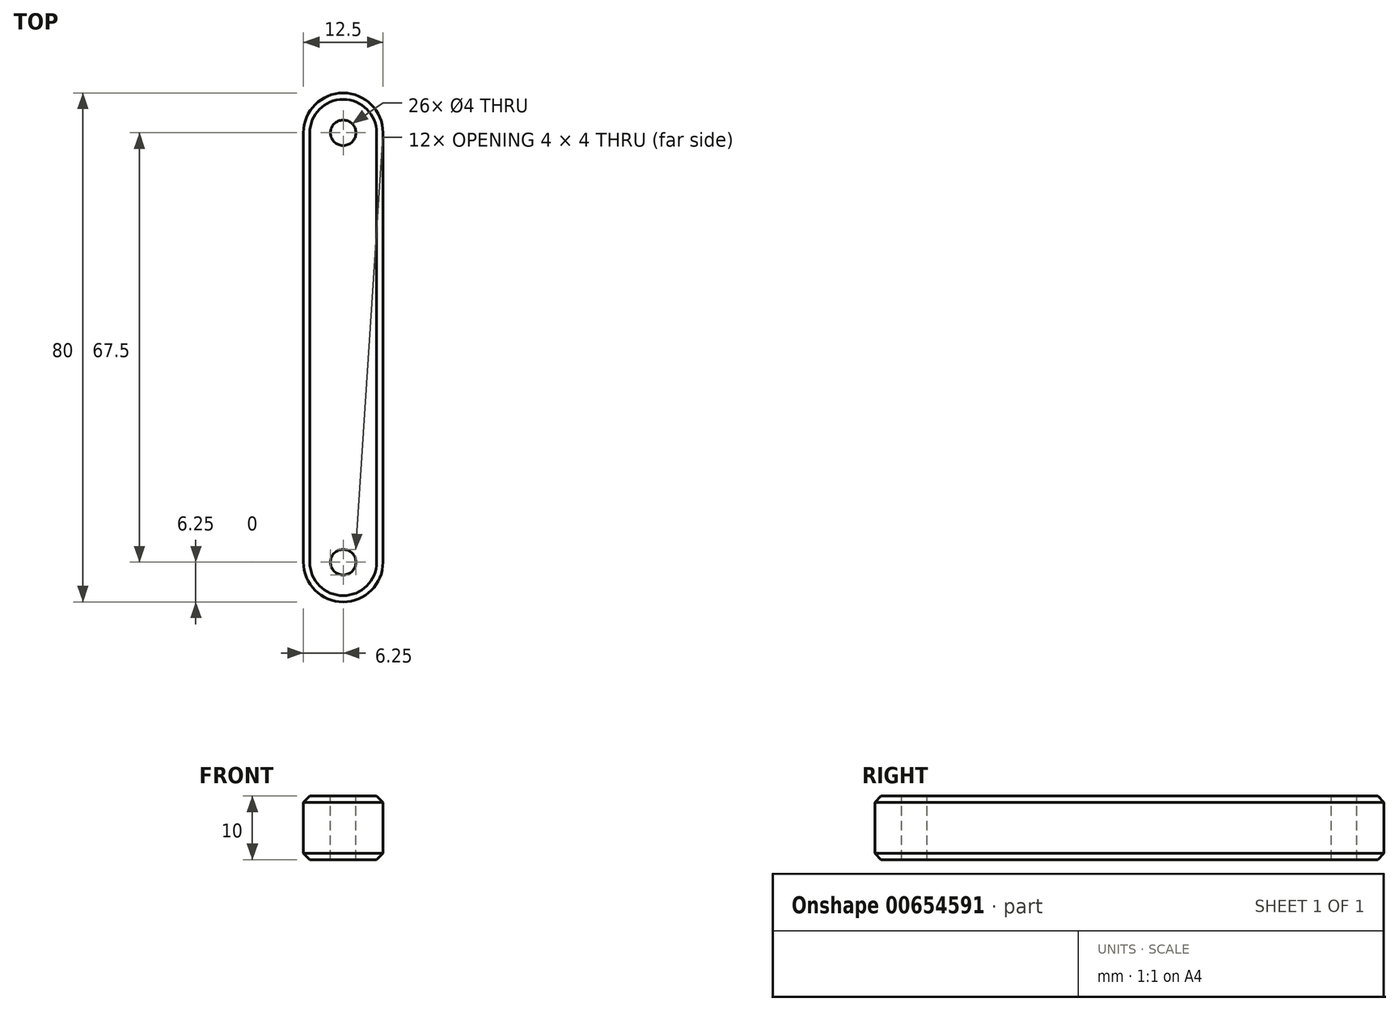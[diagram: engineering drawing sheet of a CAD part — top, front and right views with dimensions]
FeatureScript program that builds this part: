
annotation { "Feature Type Name" : "Feature", "Feature Type Description" : "" }
export const myFeature = defineFeature(function(context is Context, id is Id, definition is map)
    precondition{}
    {
        {
            var Q0;
            Q0=qCreatedBy(makeId("Front.planeOp"),FACE);
            var sketch = newSketch(context, id + "F0", { "sketchPlane" : qUnion([Q0])});
            skLineSegment(sketch, "E0.bottom", {"start": v(0, 0) * mm, "end": v(12.5, 0) * mm});
            skLineSegment(sketch, "E0.top", {"start": v(0, 10) * mm, "end": v(12.5, 10) * mm});
            skLineSegment(sketch, "E0.left", {"start": v(0, 0) * mm, "end": v(0, 10) * mm});
            skLineSegment(sketch, "E0.right", {"start": v(12.5, 0) * mm, "end": v(12.5, 10) * mm});
            skSolve(sketch);
        }
        {
            var Q0;
            Q0=makeQuery(id+"F0.imprint","IMPRINT",FACE,{"disambiguationData":[TD([[makeQuery(id+"F0.imprint","IMPRINT",EDGE,{"derivedFrom":sQuery(id+"F0.wireOp",EDGE,"E0.bottom")}),1.0]])]});
            extrude(context, id + "F1", {"entities" : qUnion([Q0]), "oppositeDirection" : true, "depth" : 80 * mm, "offsetDistance" : 25 * mm});
        }
        {
            var Q0;
            Q0=makeQuery(id+"F1.opExtrude","SWEPT_FACE",FACE,{"disambiguationData":[OSD([sQuery(id+"F0.wireOp",EDGE,"E0.top")])]});
            var sketch = newSketch(context, id + "F2", { "sketchPlane" : qUnion([Q0])});
            skCircle(sketch, "E1", {"center": v(6.25, 6.25) * mm, "radius": 2 * mm});
            skPoint(sketch, "E1.centerSnap0", {"position": v(6.25, 0) * mm});
            skCircle(sketch, "E2", {"center": v(6.25, 73.75) * mm, "radius": 2 * mm});
            skPoint(sketch, "E2.centerSnap0", {"position": v(6.25, 80) * mm});
            skSolve(sketch);
        }
        {
            var Q0;
            Q0=makeQuery(id+"F2.imprint","IMPRINT",FACE,{"disambiguationData":[TD([[makeQuery(id+"F2.imprint","IMPRINT",EDGE,{"derivedFrom":sQuery(id+"F2.wireOp",EDGE,"E2")}),1.0]])]});
            var Q1;
            Q1=makeQuery(id+"F2.imprint","IMPRINT",FACE,{"disambiguationData":[TD([[makeQuery(id+"F2.imprint","IMPRINT",EDGE,{"derivedFrom":sQuery(id+"F2.wireOp",EDGE,"E1")}),1.0]])]});
            extrude(context, id + "F3", {"entities" : qUnion([Q0, Q1]), "operationType" : NewBodyOperationType.REMOVE, "endBound" : BoundingType.UP_TO_NEXT, "oppositeDirection" : true, "depth" : 25 * mm, "offsetDistance" : 25 * mm});
        }
        {
            var Q0;
            Q0=makeQuery(id+"F1.opExtrude","CAP_EDGE",EDGE,{"disambiguationData":[OSD([sQuery(id+"F0.wireOp",EDGE,"E0.right")])],"isStart":true});
            var Q1;
            Q1=makeQuery(id+"F1.opExtrude","CAP_EDGE",EDGE,{"disambiguationData":[OSD([sQuery(id+"F0.wireOp",EDGE,"E0.left")])],"isStart":true});
            var Q2;
            Q2=makeQuery(id+"F1.opExtrude","CAP_EDGE",EDGE,{"disambiguationData":[OSD([sQuery(id+"F0.wireOp",EDGE,"E0.right")])],"isStart":false});
            var Q3;
            Q3=makeQuery(id+"F1.opExtrude","CAP_EDGE",EDGE,{"disambiguationData":[OSD([sQuery(id+"F0.wireOp",EDGE,"E0.left")])],"isStart":false});
            fillet(context, id + "F4", {"entities" : qUnion([Q0, Q1, Q2, Q3]), "radius" : 6.25 * mm, "tangentPropagation" : true, "allowEdgeOverflow" : false});
        }
        {
            var Q0;
            Q0=makeQuery(id+"F1.opExtrude","SWEPT_FACE",FACE,{"disambiguationData":[OSD([sQuery(id+"F0.wireOp",EDGE,"E0.left")])]});
            var Q1;
            {var subQ0=sQuery(id+"F0.wireOp",EDGE,"E0.right");Q1=makeQuery(id+"F4.opFillet","BLEND_FACE",FACE,{"disambiguationData":[OSD([subQ0]),TDD([makeQuery(id+"F1.opExtrude","CAP_EDGE",EDGE,{"disambiguationData":[OSD([subQ0])],"isStart":true})])]});}
            var Q2;
            Q2=makeQuery(id+"F1.opExtrude","SWEPT_FACE",FACE,{"disambiguationData":[OSD([sQuery(id+"F0.wireOp",EDGE,"E0.right")])]});
            var Q3;
            {var subQ0=sQuery(id+"F0.wireOp",EDGE,"E0.right");Q3=makeQuery(id+"F4.opFillet","BLEND_FACE",FACE,{"disambiguationData":[OSD([subQ0]),TDD([makeQuery(id+"F1.opExtrude","CAP_EDGE",EDGE,{"disambiguationData":[OSD([subQ0])],"isStart":false})])]});}
            chamfer(context, id + "F5", {"entities" : qUnion([Q0, Q1, Q2, Q3]), "width" : 1 * mm, "tangentPropagation" : true});
        }
    });
